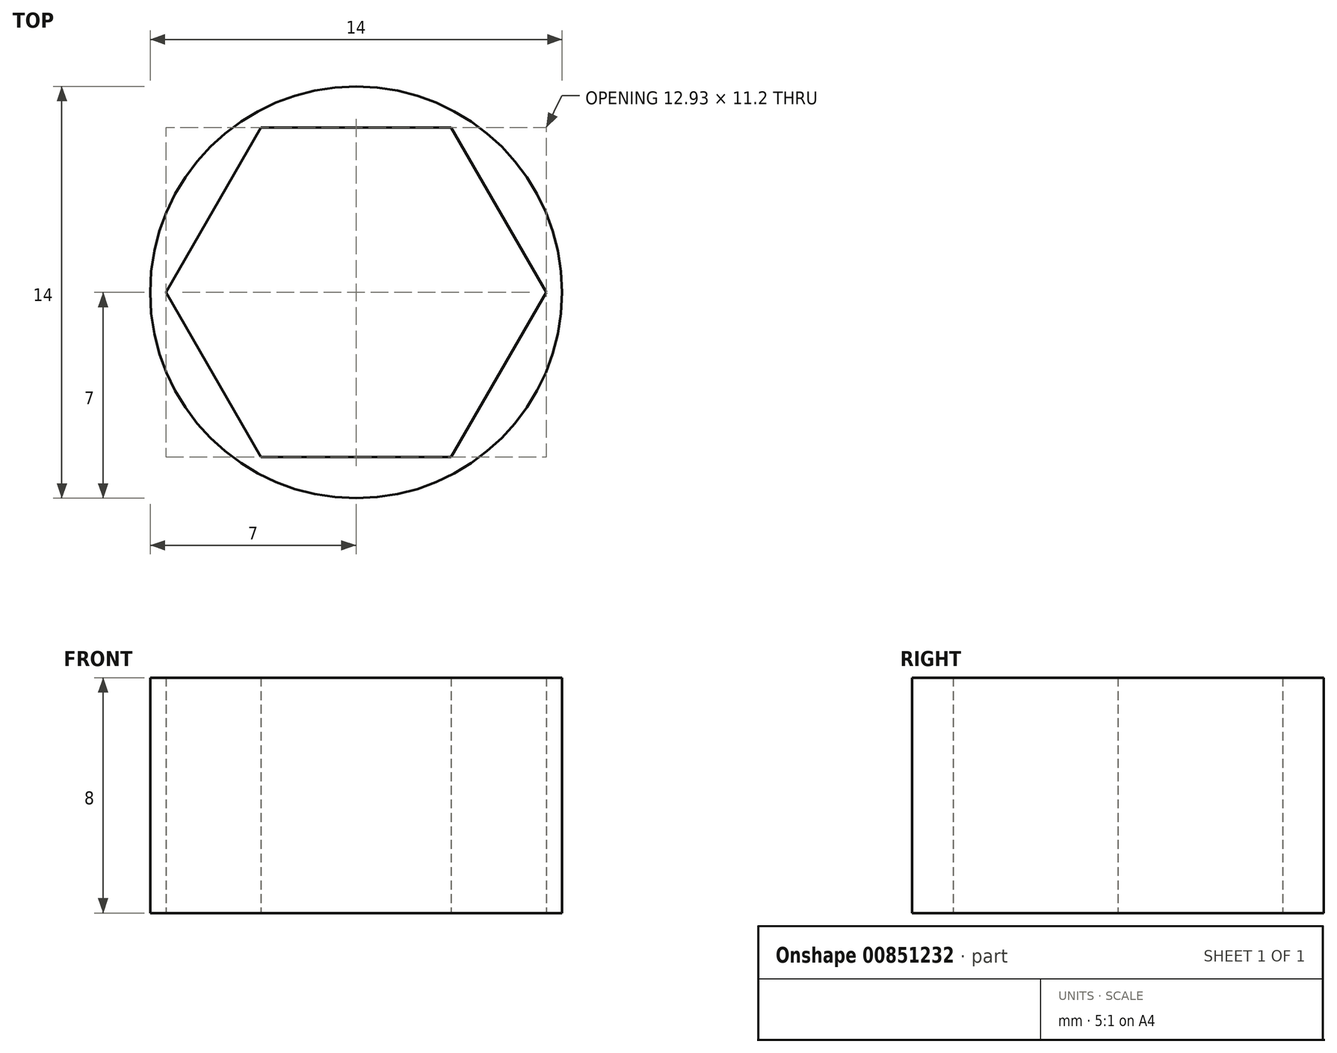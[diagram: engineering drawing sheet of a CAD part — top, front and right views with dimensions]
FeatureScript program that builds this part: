
annotation { "Feature Type Name" : "Feature", "Feature Type Description" : "" }
export const myFeature = defineFeature(function(context is Context, id is Id, definition is map)
    precondition{}
    {
        {
            var Q0;
            Q0=qCreatedBy(makeId("Top.planeOp"),FACE);
            var sketch = newSketch(context, id + "F0", { "sketchPlane" : qUnion([Q0])});
            skCircle(sketch, "E0", {"center": v(0, 0) * mm, "radius": 7 * mm});
            skCircle(sketch, "E1.cCircle", {"center": v(0, 0) * mm, "radius": 5.6 * mm, "construction": true});
            skLineSegment(sketch, "E1.0", {"start": v(-3.23, 5.6) * mm, "end": v(3.23, 5.6) * mm});
            skLineSegment(sketch, "E1.1", {"start": v(3.23, 5.6) * mm, "end": v(6.47, 0) * mm});
            skLineSegment(sketch, "E1.2", {"start": v(6.47, 0) * mm, "end": v(3.23, -5.6) * mm});
            skLineSegment(sketch, "E1.3", {"start": v(3.23, -5.6) * mm, "end": v(-3.23, -5.6) * mm});
            skLineSegment(sketch, "E1.4", {"start": v(-3.23, -5.6) * mm, "end": v(-6.47, 0) * mm});
            skLineSegment(sketch, "E1.5", {"start": v(-6.47, 0) * mm, "end": v(-3.23, 5.6) * mm});
            skPoint(sketch, "E1.0.midPoint", {"position": v(0, 5.6) * mm});
            skSolve(sketch);
        }
        {
            var Q0;
            Q0=makeQuery(id+"F0.imprint","IMPRINT",FACE,{"disambiguationData":[TD([[makeQuery(id+"F0.imprint","IMPRINT",EDGE,{"derivedFrom":sQuery(id+"F0.wireOp",EDGE,"E0")}),1.0]])]});
            extrude(context, id + "F1", {"entities" : qUnion([Q0]), "depth" : 8 * mm, "offsetDistance" : 25 * mm});
        }
    });
